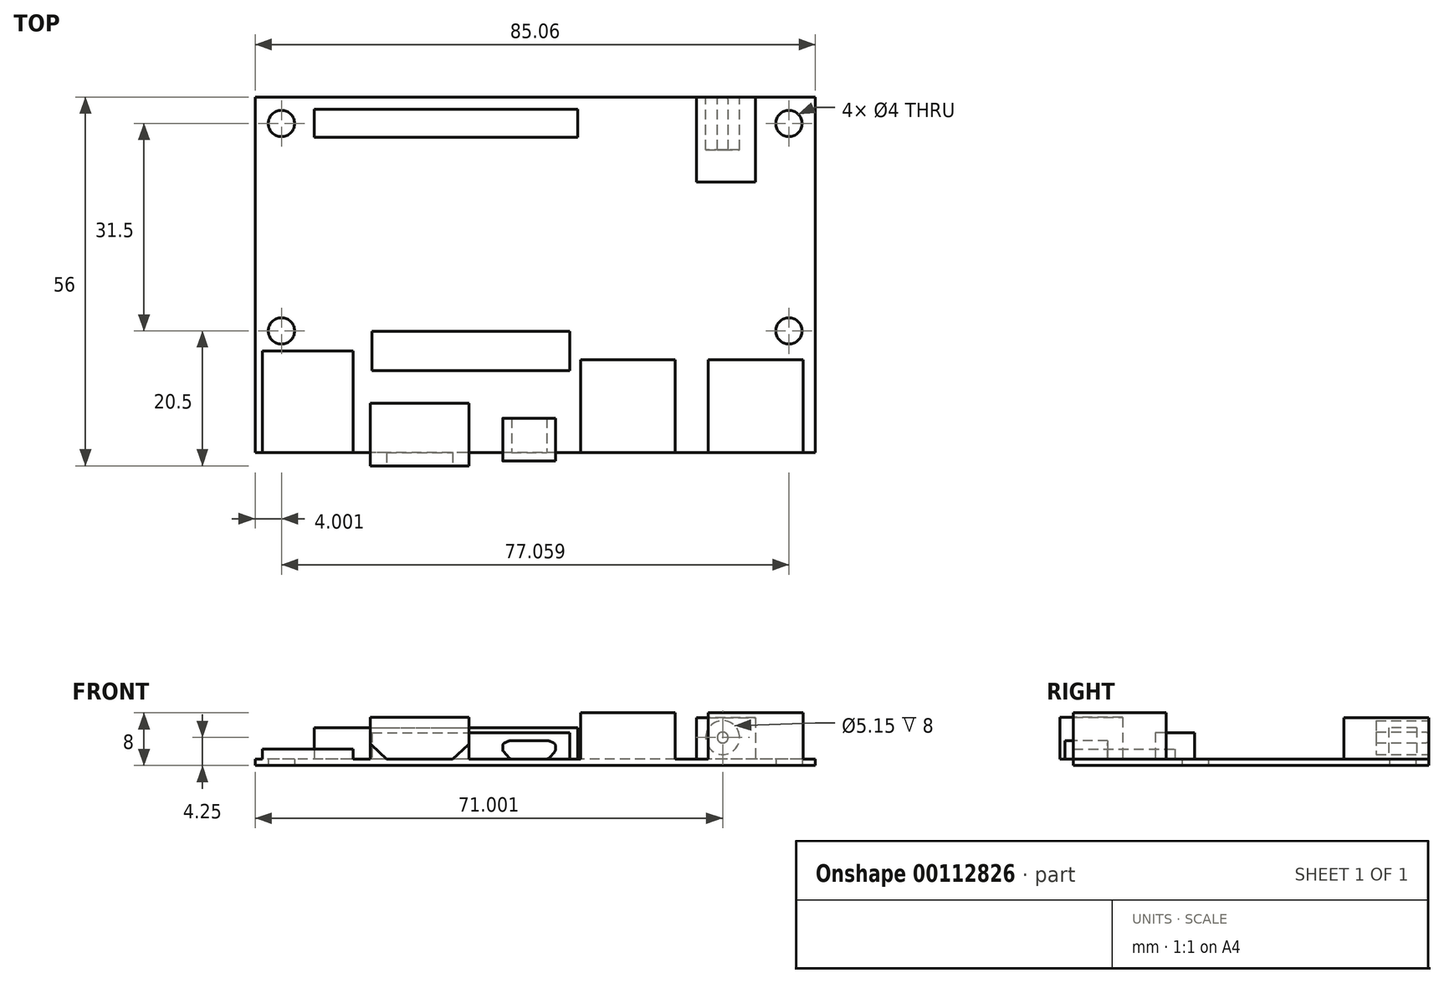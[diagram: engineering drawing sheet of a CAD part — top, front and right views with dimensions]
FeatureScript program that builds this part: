
annotation { "Feature Type Name" : "Feature", "Feature Type Description" : "" }
export const myFeature = defineFeature(function(context is Context, id is Id, definition is map)
    precondition{}
    {
        {
            var Q0;
            Q0=qCreatedBy(makeId("Top.planeOp"),FACE);
            var sketch = newSketch(context, id + "F0", { "sketchPlane" : qUnion([Q0])});
            skLineSegment(sketch, "E0.bottom", {"start": v(42.53, -27) * mm, "end": v(-42.53, -27) * mm});
            skLineSegment(sketch, "E0.top", {"start": v(42.53, 27) * mm, "end": v(-42.53, 27) * mm});
            skLineSegment(sketch, "E0.left", {"start": v(42.53, -27) * mm, "end": v(42.53, 27) * mm});
            skLineSegment(sketch, "E0.right", {"start": v(-42.53, -27) * mm, "end": v(-42.53, 27) * mm});
            skPoint(sketch, "E0.middle", {"position": v(0, 0) * mm});
            skLineSegment(sketch, "E1", {"start": v(-38.53, 27) * mm, "end": v(-38.53, -27) * mm, "construction": true});
            skLineSegment(sketch, "E2", {"start": v(38.53, 27) * mm, "end": v(38.53, -27) * mm, "construction": true});
            skLineSegment(sketch, "E3", {"start": v(-42.53, 23) * mm, "end": v(42.53, 23) * mm, "construction": true});
            skLineSegment(sketch, "E4", {"start": v(-42.53, -8.5) * mm, "end": v(42.53, -8.5) * mm, "construction": true});
            skPoint(sketch, "E5", {"position": v(-38.53, 23) * mm});
            skPoint(sketch, "E6", {"position": v(38.53, 23) * mm});
            skPoint(sketch, "E7", {"position": v(38.53, -8.5) * mm});
            skPoint(sketch, "E8", {"position": v(-38.53, -8.5) * mm});
            skCircle(sketch, "E9", {"center": v(-38.53, 23) * mm, "radius": 2 * mm});
            skCircle(sketch, "E10", {"center": v(38.53, 23) * mm, "radius": 2 * mm});
            skCircle(sketch, "E11", {"center": v(38.53, -8.5) * mm, "radius": 2 * mm});
            skCircle(sketch, "E12", {"center": v(-38.53, -8.5) * mm, "radius": 2 * mm});
            skSolve(sketch);
        }
        {
            var Q0;
            Q0=makeQuery(id+"F0.imprint","IMPRINT",FACE,{"disambiguationData":[TD([[makeQuery(id+"F0.imprint","IMPRINT",EDGE,{"derivedFrom":sQuery(id+"F0.wireOp",EDGE,"E0.bottom")}),-1.0]])]});
            var sketch = newSketch(context, id + "F1", { "sketchPlane" : qUnion([Q0])});
            skLineSegment(sketch, "E13.bottom", {"start": v(-35.03, 26.25) * mm, "end": v(7.97, 26.25) * mm, "construction": true});
            skLineSegment(sketch, "E13.top", {"start": v(-35.03, 19.75) * mm, "end": v(7.97, 19.75) * mm, "construction": true});
            skLineSegment(sketch, "E13.left", {"start": v(-35.03, 26.25) * mm, "end": v(-35.03, 19.75) * mm, "construction": true});
            skLineSegment(sketch, "E13.right", {"start": v(7.97, 26.25) * mm, "end": v(7.97, 19.75) * mm, "construction": true});
            skPoint(sketch, "E14", {"position": v(-35.03, 23) * mm});
            skLineSegment(sketch, "E15", {"start": v(-32.53, 26.25) * mm, "end": v(-32.53, 19.75) * mm, "construction": true});
            skPoint(sketch, "E16", {"position": v(-32.53, 23) * mm});
            skLineSegment(sketch, "E17.bottom", {"start": v(-33.53, 25.12) * mm, "end": v(6.47, 25.12) * mm});
            skLineSegment(sketch, "E17.top", {"start": v(-33.53, 20.88) * mm, "end": v(6.47, 20.88) * mm});
            skLineSegment(sketch, "E17.left", {"start": v(-33.53, 25.12) * mm, "end": v(-33.53, 20.87) * mm});
            skLineSegment(sketch, "E17.right", {"start": v(6.47, 25.12) * mm, "end": v(6.47, 20.87) * mm});
            skSolve(sketch);
        }
        {
            var Q0;
            Q0=makeQuery(id+"F0.imprint","IMPRINT",FACE,{"disambiguationData":[TD([[makeQuery(id+"F0.imprint","IMPRINT",EDGE,{"derivedFrom":sQuery(id+"F0.wireOp",EDGE,"E0.bottom")}),-1.0]])]});
            var sketch = newSketch(context, id + "F2", { "sketchPlane" : qUnion([Q0])});
            skLineSegment(sketch, "E18.0", {"start": v(42.53, 27) * mm, "end": v(-42.53, 27) * mm});
            skLineSegment(sketch, "E19", {"start": v(24.47, 27) * mm, "end": v(24.47, 14.1) * mm});
            skLineSegment(sketch, "E20", {"start": v(24.47, 14.1) * mm, "end": v(33.47, 14.1) * mm});
            skLineSegment(sketch, "E21", {"start": v(33.47, 14.1) * mm, "end": v(33.47, 27) * mm});
            skLineSegment(sketch, "E22", {"start": v(28.97, 14.1) * mm, "end": v(28.97, 27) * mm, "construction": true});
            skLineSegment(sketch, "E23.0", {"start": v(-42.53, -27) * mm, "end": v(-42.53, 27) * mm});
            skSolve(sketch);
        }
        {
            var Q0;
            Q0=makeQuery(id+"F0.imprint","IMPRINT",FACE,{"disambiguationData":[TD([[makeQuery(id+"F0.imprint","IMPRINT",EDGE,{"derivedFrom":sQuery(id+"F0.wireOp",EDGE,"E0.bottom")}),-1.0]])]});
            var sketch = newSketch(context, id + "F3", { "sketchPlane" : qUnion([Q0])});
            skLineSegment(sketch, "E24.0", {"start": v(-42.53, -27) * mm, "end": v(-42.53, 27) * mm});
            skLineSegment(sketch, "E25.0", {"start": v(42.53, -27) * mm, "end": v(42.53, 27) * mm});
            skLineSegment(sketch, "E26", {"start": v(-42.53, -11.55) * mm, "end": v(42.53, -11.55) * mm, "construction": true});
            skLineSegment(sketch, "E27.0", {"start": v(42.53, -27) * mm, "end": v(-42.53, -27) * mm});
            skLineSegment(sketch, "E28", {"start": v(-34.53, -27) * mm, "end": v(-34.53, -11.55) * mm, "construction": true});
            skLineSegment(sketch, "E29", {"start": v(-17.53, -27) * mm, "end": v(-17.53, -11.55) * mm, "construction": true});
            skLineSegment(sketch, "E30", {"start": v(-25.03, -27) * mm, "end": v(-25.03, -19.5) * mm});
            skLineSegment(sketch, "E31", {"start": v(-25.03, -19.5) * mm, "end": v(-10.03, -19.5) * mm});
            skLineSegment(sketch, "E32", {"start": v(-10.03, -19.5) * mm, "end": v(-10.03, -27) * mm});
            skLineSegment(sketch, "E33", {"start": v(-41.41, -27) * mm, "end": v(-41.41, -11.55) * mm});
            skLineSegment(sketch, "E34", {"start": v(-41.41, -11.55) * mm, "end": v(-27.64, -11.55) * mm});
            skLineSegment(sketch, "E35", {"start": v(-27.64, -11.55) * mm, "end": v(-27.64, -27) * mm});
            skLineSegment(sketch, "E36", {"start": v(-0.93, -11.55) * mm, "end": v(-0.93, -27) * mm, "construction": true});
            skLineSegment(sketch, "E37", {"start": v(-4.93, -27) * mm, "end": v(-4.93, -21.75) * mm});
            skLineSegment(sketch, "E38", {"start": v(-4.93, -21.75) * mm, "end": v(3.07, -21.75) * mm});
            skLineSegment(sketch, "E39", {"start": v(3.07, -21.75) * mm, "end": v(3.07, -27) * mm});
            skLineSegment(sketch, "E40", {"start": v(14.07, -27) * mm, "end": v(14.07, -11.55) * mm, "construction": true});
            skLineSegment(sketch, "E41", {"start": v(33.47, -27) * mm, "end": v(33.47, -11.55) * mm, "construction": true});
            skLineSegment(sketch, "E42", {"start": v(6.87, -27) * mm, "end": v(6.87, -12.9) * mm});
            skLineSegment(sketch, "E43", {"start": v(6.87, -12.9) * mm, "end": v(21.27, -12.9) * mm});
            skLineSegment(sketch, "E44", {"start": v(21.27, -12.9) * mm, "end": v(21.27, -27) * mm});
            skLineSegment(sketch, "E45", {"start": v(26.27, -27) * mm, "end": v(26.27, -12.9) * mm});
            skLineSegment(sketch, "E46", {"start": v(26.27, -12.9) * mm, "end": v(40.67, -12.9) * mm});
            skLineSegment(sketch, "E47", {"start": v(40.67, -12.9) * mm, "end": v(40.67, -27) * mm});
            skLineSegment(sketch, "E48", {"start": v(-25.03, -27) * mm, "end": v(-25.03, -29) * mm});
            skLineSegment(sketch, "E49", {"start": v(-25.03, -29) * mm, "end": v(-10.03, -29) * mm});
            skLineSegment(sketch, "E50", {"start": v(-10.03, -29) * mm, "end": v(-10.03, -27) * mm});
            skLineSegment(sketch, "E51", {"start": v(-4.93, -27) * mm, "end": v(-4.93, -28.25) * mm});
            skLineSegment(sketch, "E52", {"start": v(-4.93, -28.25) * mm, "end": v(3.07, -28.25) * mm});
            skLineSegment(sketch, "E53", {"start": v(3.07, -28.25) * mm, "end": v(3.07, -27) * mm});
            skSolve(sketch);
        }
        {
            var Q0;
            Q0=makeQuery(id+"F0.imprint","IMPRINT",FACE,{"disambiguationData":[TD([[makeQuery(id+"F0.imprint","IMPRINT",EDGE,{"derivedFrom":sQuery(id+"F0.wireOp",EDGE,"E0.bottom")}),-1.0]])]});
            var sketch = newSketch(context, id + "F4", { "sketchPlane" : qUnion([Q0])});
            skLineSegment(sketch, "E54.bottom", {"start": v(-24.76, -8.55) * mm, "end": v(5.24, -8.55) * mm});
            skLineSegment(sketch, "E54.top", {"start": v(-24.76, -14.55) * mm, "end": v(5.24, -14.55) * mm});
            skLineSegment(sketch, "E54.left", {"start": v(-24.76, -8.55) * mm, "end": v(-24.76, -14.55) * mm});
            skLineSegment(sketch, "E54.right", {"start": v(5.24, -8.55) * mm, "end": v(5.24, -14.55) * mm});
            skLineSegment(sketch, "E55.0", {"start": v(-21.38, -27) * mm, "end": v(-21.38, -11.55) * mm});
            skLineSegment(sketch, "E55.1", {"start": v(-42.53, -27) * mm, "end": v(-42.53, 27) * mm});
            skSolve(sketch);
        }
        {
            var Q0;
            Q0 = qSketchRegion(id + "F0", true);
            extrude(context, id + "F5", {"entities" : qUnion([Q0]), "depth" : 1 * mm});
        }
        {
            var Q0;
            {var subQ0=sQuery(id+"F3.wireOp",EDGE,"E45");Q0=makeQuery(id+"F3.imprint","IMPRINT",FACE,{"disambiguationData":[TD([[makeQuery(id+"F3.imprint","IMPRINT",EDGE,{"derivedFrom":subQ0}),-1.0]])]});}
            var Q1;
            {var subQ0=sQuery(id+"F3.wireOp",EDGE,"E42");Q1=makeQuery(id+"F3.imprint","IMPRINT",FACE,{"disambiguationData":[TD([[makeQuery(id+"F3.imprint","IMPRINT",EDGE,{"derivedFrom":subQ0}),-1.0]])]});}
            extrude(context, id + "F6", {"entities" : qUnion([Q0, Q1]), "operationType" : NewBodyOperationType.ADD, "depth" : 8 * mm});
        }
        {
            var Q0;
            {var subQ0=sQuery(id+"F3.wireOp",EDGE,"E51");Q0=makeQuery(id+"F3.imprint","IMPRINT",FACE,{"disambiguationData":[TD([[makeQuery(id+"F3.imprint","IMPRINT",EDGE,{"derivedFrom":subQ0}),1.0]])]});}
            var Q1;
            {var subQ0=sQuery(id+"F3.wireOp",EDGE,"E37");Q1=makeQuery(id+"F3.imprint","IMPRINT",FACE,{"disambiguationData":[TD([[makeQuery(id+"F3.imprint","IMPRINT",EDGE,{"derivedFrom":subQ0}),-1.0]])]});}
            extrude(context, id + "F7", {"entities" : qUnion([Q0, Q1]), "operationType" : NewBodyOperationType.ADD, "depth" : 3.75 * mm});
        }
        {
            var Q0;
            {var subQ0=sQuery(id+"F3.wireOp",EDGE,"E48");Q0=makeQuery(id+"F3.imprint","IMPRINT",FACE,{"disambiguationData":[TD([[makeQuery(id+"F3.imprint","IMPRINT",EDGE,{"derivedFrom":subQ0}),1.0]])]});}
            var Q1;
            {var subQ0=sQuery(id+"F3.wireOp",EDGE,"E30");Q1=makeQuery(id+"F3.imprint","IMPRINT",FACE,{"disambiguationData":[TD([[makeQuery(id+"F3.imprint","IMPRINT",EDGE,{"derivedFrom":subQ0}),-1.0]])]});}
            extrude(context, id + "F8", {"entities" : qUnion([Q0, Q1]), "operationType" : NewBodyOperationType.ADD, "depth" : 7.3 * mm});
        }
        {
            var Q0;
            {var subQ0=sQuery(id+"F3.wireOp",EDGE,"E33");Q0=makeQuery(id+"F3.imprint","IMPRINT",FACE,{"disambiguationData":[TD([[makeQuery(id+"F3.imprint","IMPRINT",EDGE,{"derivedFrom":subQ0}),-1.0]])]});}
            extrude(context, id + "F9", {"entities" : qUnion([Q0]), "operationType" : NewBodyOperationType.ADD, "depth" : 2.5 * mm});
        }
        {
            var Q0;
            {var subQ0=sQuery(id+"F2.wireOp",EDGE,"E19");Q0=makeQuery(id+"F2.imprint","IMPRINT",FACE,{"disambiguationData":[TD([[makeQuery(id+"F2.imprint","IMPRINT",EDGE,{"derivedFrom":subQ0}),1.0]])]});}
            extrude(context, id + "F10", {"entities" : qUnion([Q0]), "operationType" : NewBodyOperationType.ADD, "depth" : 7.25 * mm});
        }
        {
            var Q0;
            Q0 = qSketchRegion(id + "F1", true);
            extrude(context, id + "F11", {"entities" : qUnion([Q0]), "operationType" : NewBodyOperationType.ADD, "depth" : 5.75 * mm});
        }
        {
            var Q0;
            Q0 = qSketchRegion(id + "F4", true);
            extrude(context, id + "F12", {"entities" : qUnion([Q0]), "operationType" : NewBodyOperationType.ADD, "depth" : 5 * mm});
        }
        {
            var Q0;
            Q0=makeQuery(id+"F7.opExtrude","SWEPT_FACE",FACE,{"disambiguationData":[OSD([sQuery(id+"F3.wireOp",EDGE,"E52")])]});
            var sketch = newSketch(context, id + "F13", { "sketchPlane" : qUnion([Q0])});
            skPoint(sketch, "E56", {"position": v(-0.93, 0) * mm});
            skLineSegment(sketch, "E57", {"start": v(-4.93, 0) * mm, "end": v(-0.93, 0) * mm, "construction": true});
            skPoint(sketch, "E58", {"position": v(-2.93, 0) * mm});
            skLineSegment(sketch, "E59", {"start": v(-0.93, 0) * mm, "end": v(3.07, 0) * mm, "construction": true});
            skPoint(sketch, "E60", {"position": v(1.07, 0) * mm});
            skLineSegment(sketch, "E61", {"start": v(-4.8, 2.1) * mm, "end": v(-3.97, 1.17) * mm});
            skLineSegment(sketch, "E62", {"start": v(2.12, 1.17) * mm, "end": v(2.94, 2.08) * mm});
            skPoint(sketch, "E63", {"position": v(-3.94, 3.75) * mm});
            skPoint(sketch, "E64", {"position": v(2.09, 3.75) * mm});
            skLineSegment(sketch, "E65", {"start": v(-0.93, 0) * mm, "end": v(-0.93, 3.75) * mm, "construction": true});
            skLineSegment(sketch, "E66", {"start": v(-4.62, 3.47) * mm, "end": v(-4.08, 3.7) * mm});
            skLineSegment(sketch, "E67", {"start": v(2.77, 3.46) * mm, "end": v(2.22, 3.7) * mm});
            skLineSegment(sketch, "E68", {"start": v(-4.93, 2.24) * mm, "end": v(3.07, 2.22) * mm, "construction": true});
            skLineSegment(sketch, "E69", {"start": v(-4.93, 3.35) * mm, "end": v(3.07, 3.33) * mm, "construction": true});
            skLineSegment(sketch, "E70", {"start": v(-4.93, 3.01) * mm, "end": v(-4.93, 2.43) * mm});
            skLineSegment(sketch, "E71", {"start": v(3.07, 3) * mm, "end": v(3.07, 2.42) * mm});
            skLineSegment(sketch, "E72", {"start": v(-3.8, 3.75) * mm, "end": v(1.94, 3.75) * mm});
            skLineSegment(sketch, "E73", {"start": v(-2.73, 0) * mm, "end": v(0.87, 0) * mm});
            skPoint(sketch, "E74.visualSharp", {"position": v(3.07, 2.22) * mm});
            skArc(sketch, "E74.filletArc", {"start": v(2.94, 2.08) * mm, "mid": v(3.04, 2.24) * mm, "end": v(3.07, 2.42) * mm});
            skPoint(sketch, "E75.visualSharp", {"position": v(3.07, 3.33) * mm});
            skArc(sketch, "E75.filletArc", {"start": v(3.07, 3) * mm, "mid": v(2.99, 3.28) * mm, "end": v(2.77, 3.46) * mm});
            skArc(sketch, "E76.filletArc", {"start": v(2.22, 3.7) * mm, "mid": v(2.08, 3.74) * mm, "end": v(1.94, 3.75) * mm});
            skArc(sketch, "E77.filletArc", {"start": v(-3.8, 3.75) * mm, "mid": v(-3.94, 3.74) * mm, "end": v(-4.08, 3.7) * mm});
            skPoint(sketch, "E78.visualSharp", {"position": v(-4.93, 3.35) * mm});
            skArc(sketch, "E78.filletArc", {"start": v(-4.62, 3.47) * mm, "mid": v(-4.84, 3.3) * mm, "end": v(-4.93, 3.01) * mm});
            skPoint(sketch, "E79.visualSharp", {"position": v(-4.93, 2.24) * mm});
            skArc(sketch, "E79.filletArc", {"start": v(-4.93, 2.43) * mm, "mid": v(-4.9, 2.25) * mm, "end": v(-4.8, 2.1) * mm});
            skLineSegment(sketch, "E80.0", {"start": v(24.47, 1) * mm, "end": v(-42.53, 1) * mm});
            skLineSegment(sketch, "E81", {"start": v(-3.6, 1) * mm, "end": v(1.75, 1) * mm});
            skPoint(sketch, "E82.visualSharp", {"position": v(-3.82, 1) * mm});
            skArc(sketch, "E82.filletArc", {"start": v(-3.97, 1.17) * mm, "mid": v(-3.8, 1.04) * mm, "end": v(-3.6, 1) * mm});
            skPoint(sketch, "E83.visualSharp", {"position": v(1.97, 1) * mm});
            skArc(sketch, "E83.filletArc", {"start": v(1.75, 1) * mm, "mid": v(1.95, 1.04) * mm, "end": v(2.12, 1.17) * mm});
            skSolve(sketch);
        }
        {
            var Q0;
            Q0=makeQuery(id+"F13.imprint","IMPRINT",FACE,{"disambiguationData":[TD([[makeQuery(id+"F13.imprint","IMPRINT",EDGE,{"derivedFrom":sQuery(id+"F13.wireOp",EDGE,"E61")}),-1.0]])]});
            var Q1;
            Q1=makeQuery(id+"F13.imprint","IMPRINT",FACE,{"disambiguationData":[TD([[makeQuery(id+"F13.imprint","IMPRINT",EDGE,{"derivedFrom":sQuery(id+"F13.wireOp",EDGE,"E66")}),1.0]])]});
            var Q2;
            Q2=makeQuery(id+"F13.imprint","IMPRINT",FACE,{"disambiguationData":[TD([[makeQuery(id+"F13.imprint","IMPRINT",EDGE,{"derivedFrom":sQuery(id+"F13.wireOp",EDGE,"E67")}),-1.0]])]});
            var Q3;
            Q3=makeQuery(id+"F13.imprint","IMPRINT",FACE,{"disambiguationData":[TD([[makeQuery(id+"F13.imprint","IMPRINT",EDGE,{"derivedFrom":sQuery(id+"F13.wireOp",EDGE,"E62")}),-1.0]])]});
            var Q4;
            {var subQ8=sQuery(id+"F13.wireOp",EDGE,"a18c98a6-a4a7-4cf6-845e-3db316127b87.filletArc");Q4=makeQuery(id+"F13.imprint","IMPRINT",FACE,{"disambiguationData":[TD([[makeQuery(id+"F13.imprint","IMPRINT",EDGE,{"derivedFrom":subQ8}),-1.0]])]});}
            var Q5;
            {var subQ6=sQuery(id+"F13.wireOp",EDGE,"c999dc16-cddd-47d2-9ace-dcb4409ff7b4.filletArc");Q5=makeQuery(id+"F13.imprint","IMPRINT",FACE,{"disambiguationData":[TD([[makeQuery(id+"F13.imprint","IMPRINT",EDGE,{"derivedFrom":subQ6}),-1.0]])]});}
            var Q6;
            {var subQ9=sQuery(id+"F13.wireOp",EDGE,"E73");Q6=makeQuery(id+"F13.imprint","IMPRINT",FACE,{"disambiguationData":[TD([[makeQuery(id+"F13.imprint","IMPRINT",EDGE,{"derivedFrom":subQ9}),1.0]])]});}
            var Q7;
            {var subQ0=sQuery(id+"F3.wireOp",EDGE,"E51");var subQ1=sQuery(id+"F3.wireOp",EDGE,"E37");var subQ2=makeQuery(id+"F7.opExtrude","SWEPT_FACE",FACE,{"disambiguationData":[OSD([subQ1,subQ0])]});var subQ8=sQuery(id+"F0.wireOp",EDGE,"E0.right");var subQ11=sQuery(id+"F0.wireOp",EDGE,"E0.bottom");var subQ16=sQuery(id+"F3.wireOp",EDGE,"E27.0");Q7=makeQuery(id+"F8.boolean.opBoolean","SPLIT",FACE,{"disambiguationData":[TD([subQ2])],"derivedFrom":makeQuery(id+"F7.boolean.opBoolean","SPLIT",FACE,{"disambiguationData":[TD([makeQuery(id+"F5.opExtrude","SWEPT_FACE",FACE,{"disambiguationData":[OSD([subQ8])]})])],"derivedFrom":makeQuery(id+"F6.boolean.opBoolean","MERGE",FACE,{"derivedFrom":[makeQuery(id+"F5.opExtrude","SWEPT_FACE",FACE,{"disambiguationData":[OSD([subQ11])]}),makeQuery(id+"F6.opExtrude","SWEPT_FACE",FACE,{"disambiguationData":[OSD([subQ16]),TDD([makeQuery(id+"F3.imprint","IMPRINT",EDGE,{"disambiguationData":[TD([[makeQuery(id+"F3.imprint","INTERSECT",VERTEX,{"derivedFrom":[subQ16,sQuery(id+"F3.wireOp",EDGE,"E45")]}),1.0]])],"derivedFrom":subQ16})])]}),makeQuery(id+"F6.opExtrude","SWEPT_FACE",FACE,{"disambiguationData":[OSD([subQ16]),TDD([makeQuery(id+"F3.imprint","IMPRINT",EDGE,{"disambiguationData":[TD([[makeQuery(id+"F3.imprint","INTERSECT",VERTEX,{"derivedFrom":[subQ16,sQuery(id+"F3.wireOp",EDGE,"E42")]}),1.0]])],"derivedFrom":subQ16})])]})]})})});}
            extrude(context, id + "F14", {"entities" : qUnion([Q0, Q1, Q2, Q3, Q4, Q5, Q6]), "operationType" : NewBodyOperationType.REMOVE, "endBound" : BoundingType.UP_TO_SURFACE, "oppositeDirection" : true, "endBoundEntityFace" : qUnion([Q7]), "depth" : 25 * mm});
        }
        {
            var Q0;
            Q0=makeQuery(id+"F14.boolean.opBoolean","COPY",FACE,{"derivedFrom":makeQuery(id+"F14.opExtrude","CAP_FACE",FACE,{"disambiguationData":[OSD([sQuery(id+"F3.wireOp",EDGE,"E51"),sQuery(id+"F3.wireOp",EDGE,"E52"),sQuery(id+"F13.wireOp",EDGE,"E66"),sQuery(id+"F13.wireOp",EDGE,"E77.filletArc"),sQuery(id+"F13.wireOp",EDGE,"E78.filletArc")])],"isStart":false})});
            var Q1;
            Q1=makeQuery(id+"F14.boolean.opBoolean","COPY",FACE,{"derivedFrom":makeQuery(id+"F14.opExtrude","CAP_FACE",FACE,{"disambiguationData":[OSD([sQuery(id+"F3.wireOp",EDGE,"E52"),sQuery(id+"F3.wireOp",EDGE,"E53"),sQuery(id+"F13.wireOp",EDGE,"E67"),sQuery(id+"F13.wireOp",EDGE,"E75.filletArc"),sQuery(id+"F13.wireOp",EDGE,"E76.filletArc")])],"isStart":false})});
            var Q2;
            {var subQ0=sQuery(id+"F13.wireOp",EDGE,"E79.filletArc");Q2=makeQuery(id+"F13.imprint","IMPRINT",FACE,{"disambiguationData":[TD([[makeQuery(id+"F13.imprint","IMPRINT",EDGE,{"derivedFrom":subQ0}),-1.0]])]});}
            var Q3;
            {var subQ0=sQuery(id+"F13.wireOp",EDGE,"E74.filletArc");Q3=makeQuery(id+"F13.imprint","IMPRINT",FACE,{"disambiguationData":[TD([[makeQuery(id+"F13.imprint","IMPRINT",EDGE,{"derivedFrom":subQ0}),-1.0]])]});}
            var Q4;
            Q4=makeQuery(id+"F7.opExtrude","SWEPT_FACE",FACE,{"disambiguationData":[OSD([sQuery(id+"F3.wireOp",EDGE,"E38")])]});
            extrude(context, id + "F15", {"entities" : qUnion([Q0, Q1, Q2, Q3]), "operationType" : NewBodyOperationType.REMOVE, "endBound" : BoundingType.UP_TO_SURFACE, "oppositeDirection" : true, "endBoundEntityFace" : qUnion([Q4]), "depth" : 25 * mm});
        }
        {
            var Q0;
            Q0=makeQuery(id+"F8.opExtrude","SWEPT_FACE",FACE,{"disambiguationData":[OSD([sQuery(id+"F3.wireOp",EDGE,"E49")])]});
            var sketch = newSketch(context, id + "F16", { "sketchPlane" : qUnion([Q0])});
            skLineSegment(sketch, "E84.0", {"start": v(-25.03, 7.3) * mm, "end": v(-10.03, 7.3) * mm});
            skLineSegment(sketch, "E85.0", {"start": v(-10.03, 7.3) * mm, "end": v(-10.03, 3.52) * mm});
            skLineSegment(sketch, "E86.0", {"start": v(-25.03, 7.3) * mm, "end": v(-25.03, 3.52) * mm});
            skLineSegment(sketch, "E87.0", {"start": v(24.47, 1) * mm, "end": v(-42.53, 1) * mm});
            skLineSegment(sketch, "E88.0", {"start": v(-25.03, 0) * mm, "end": v(-10.03, 0) * mm});
            skLineSegment(sketch, "E89", {"start": v(-17.53, 7.3) * mm, "end": v(-17.53, 1) * mm, "construction": true});
            skPoint(sketch, "E90", {"position": v(-12.53, 1) * mm});
            skPoint(sketch, "E91", {"position": v(-22.53, 1) * mm});
            skLineSegment(sketch, "E92", {"start": v(-24.87, 3.15) * mm, "end": v(-22.53, 1) * mm});
            skLineSegment(sketch, "E93", {"start": v(-12.53, 1) * mm, "end": v(-10.2, 3.15) * mm});
            skLineSegment(sketch, "E94.trimOffspring", {"start": v(-10.03, 1) * mm, "end": v(-10.03, 0) * mm});
            skLineSegment(sketch, "E95.trimOffspring", {"start": v(-25.03, 1) * mm, "end": v(-25.03, 0) * mm});
            skPoint(sketch, "E96.visualSharp", {"position": v(-25.03, 3.3) * mm});
            skArc(sketch, "E96.filletArc", {"start": v(-25.03, 3.52) * mm, "mid": v(-24.99, 3.32) * mm, "end": v(-24.87, 3.15) * mm});
            skPoint(sketch, "E97.visualSharp", {"position": v(-10.03, 3.3) * mm});
            skArc(sketch, "E97.filletArc", {"start": v(-10.2, 3.15) * mm, "mid": v(-10.07, 3.32) * mm, "end": v(-10.03, 3.52) * mm});
            skSolve(sketch);
        }
        {
            var Q0;
            {var subQ0=sQuery(id+"F16.wireOp",EDGE,"E92");Q0=makeQuery(id+"F16.imprint","IMPRINT",FACE,{"disambiguationData":[TD([[makeQuery(id+"F16.imprint","IMPRINT",EDGE,{"derivedFrom":subQ0}),-1.0]])]});}
            var Q1;
            {var subQ0=sQuery(id+"F16.wireOp",EDGE,"E93");Q1=makeQuery(id+"F16.imprint","IMPRINT",FACE,{"disambiguationData":[TD([[makeQuery(id+"F16.imprint","IMPRINT",EDGE,{"derivedFrom":subQ0}),-1.0]])]});}
            var Q2;
            {var subQ3=sQuery(id+"F16.wireOp",EDGE,"E88.0");Q2=makeQuery(id+"F16.imprint","IMPRINT",FACE,{"disambiguationData":[TD([[makeQuery(id+"F16.imprint","IMPRINT",EDGE,{"derivedFrom":subQ3}),1.0]])]});}
            var Q3;
            {var subQ0=sQuery(id+"F3.wireOp",EDGE,"E53");var subQ1=sQuery(id+"F3.wireOp",EDGE,"E52");var subQ2=sQuery(id+"F3.wireOp",EDGE,"E51");var subQ3=sQuery(id+"F3.wireOp",EDGE,"E37");var subQ4=makeQuery(id+"F7.opExtrude","SWEPT_FACE",FACE,{"disambiguationData":[OSD([subQ3,subQ2])]});var subQ11=sQuery(id+"F0.wireOp",EDGE,"E0.right");var subQ12=sQuery(id+"F0.wireOp",EDGE,"E0.left");var subQ14=sQuery(id+"F0.wireOp",EDGE,"E0.bottom");var subQ19=sQuery(id+"F3.wireOp",EDGE,"E42");var subQ20=sQuery(id+"F3.wireOp",EDGE,"E27.0");var subQ22=sQuery(id+"F3.wireOp",EDGE,"E45");var subQ24=makeQuery(id+"F6.boolean.opBoolean","MERGE",FACE,{"derivedFrom":[makeQuery(id+"F5.opExtrude","SWEPT_FACE",FACE,{"disambiguationData":[OSD([subQ14])]}),makeQuery(id+"F6.opExtrude","SWEPT_FACE",FACE,{"disambiguationData":[OSD([subQ20]),TDD([makeQuery(id+"F3.imprint","IMPRINT",EDGE,{"disambiguationData":[TD([[makeQuery(id+"F3.imprint","INTERSECT",VERTEX,{"derivedFrom":[subQ20,subQ22]}),1.0]])],"derivedFrom":subQ20})])]}),makeQuery(id+"F6.opExtrude","SWEPT_FACE",FACE,{"disambiguationData":[OSD([subQ20]),TDD([makeQuery(id+"F3.imprint","IMPRINT",EDGE,{"disambiguationData":[TD([[makeQuery(id+"F3.imprint","INTERSECT",VERTEX,{"derivedFrom":[subQ20,subQ19]}),1.0]])],"derivedFrom":subQ20})])]})]});Q3=makeQuery(id+"F14.boolean.opBoolean","MERGE",FACE,{"derivedFrom":[makeQuery(id+"F7.boolean.opBoolean","SPLIT",FACE,{"disambiguationData":[TD([makeQuery(id+"F5.opExtrude","SWEPT_FACE",FACE,{"disambiguationData":[OSD([subQ12])]})])],"derivedFrom":subQ24}),makeQuery(id+"F8.boolean.opBoolean","SPLIT",FACE,{"disambiguationData":[TD([subQ4])],"derivedFrom":makeQuery(id+"F7.boolean.opBoolean","SPLIT",FACE,{"disambiguationData":[TD([makeQuery(id+"F5.opExtrude","SWEPT_FACE",FACE,{"disambiguationData":[OSD([subQ11])]})])],"derivedFrom":subQ24})}),makeQuery(id+"F14.opExtrude","CAP_FACE",FACE,{"disambiguationData":[OSD([subQ2,subQ1,subQ0,sQuery(id+"F13.wireOp",EDGE,"E61"),sQuery(id+"F13.wireOp",EDGE,"E62"),sQuery(id+"F13.wireOp",EDGE,"E73"),sQuery(id+"F13.wireOp",EDGE,"E74.filletArc"),sQuery(id+"F13.wireOp",EDGE,"E79.filletArc"),sQuery(id+"F13.wireOp",EDGE,"E81"),sQuery(id+"F13.wireOp",EDGE,"E82.filletArc"),sQuery(id+"F13.wireOp",EDGE,"E83.filletArc")])],"isStart":false})]});}
            extrude(context, id + "F17", {"entities" : qUnion([Q0, Q1, Q2]), "operationType" : NewBodyOperationType.REMOVE, "endBound" : BoundingType.UP_TO_SURFACE, "oppositeDirection" : true, "endBoundEntityFace" : qUnion([Q3]), "depth" : 25 * mm});
        }
        {
            var Q0;
            Q0=makeQuery(id+"F10.boolean.opBoolean","MERGE",FACE,{"derivedFrom":[makeQuery(id+"F5.opExtrude","SWEPT_FACE",FACE,{"disambiguationData":[OSD([sQuery(id+"F0.wireOp",EDGE,"E0.top")])]}),makeQuery(id+"F10.opExtrude","SWEPT_FACE",FACE,{"disambiguationData":[OSD([sQuery(id+"F2.wireOp",EDGE,"E18.0")])]})]});
            var sketch = newSketch(context, id + "F18", { "sketchPlane" : qUnion([Q0])});
            skLineSegment(sketch, "E98", {"start": v(-28.47, 7.25) * mm, "end": v(-28.47, 1) * mm, "construction": true});
            skCircle(sketch, "E99", {"center": v(-28.47, 4.25) * mm, "radius": 2.58 * mm});
            skCircle(sketch, "E100", {"center": v(-28.47, 4.25) * mm, "radius": 0.82 * mm});
            skLineSegment(sketch, "E101", {"start": v(-33.47, 7.25) * mm, "end": v(-24.47, 7.25) * mm});
            skSolve(sketch);
        }
        {
            var Q0;
            Q0=makeQuery(id+"F18.imprint","IMPRINT",FACE,{"disambiguationData":[TD([[makeQuery(id+"F18.imprint","IMPRINT",EDGE,{"derivedFrom":sQuery(id+"F18.wireOp",EDGE,"E99")}),1.0]])]});
            extrude(context, id + "F19", {"entities" : qUnion([Q0]), "operationType" : NewBodyOperationType.REMOVE, "oppositeDirection" : true, "depth" : 8 * mm});
        }
        {
            var Q0;
            Q0=makeQuery(id+"F19.boolean.opBoolean","SPLIT",FACE,{"disambiguationData":[TD([makeQuery(id+"F19.opExtrude","SWEPT_FACE",FACE,{"disambiguationData":[OSD([sQuery(id+"F18.wireOp",EDGE,"E100")])]})])],"derivedFrom":makeQuery(id+"F10.boolean.opBoolean","MERGE",FACE,{"derivedFrom":[makeQuery(id+"F5.opExtrude","SWEPT_FACE",FACE,{"disambiguationData":[OSD([sQuery(id+"F0.wireOp",EDGE,"E0.top")])]}),makeQuery(id+"F10.opExtrude","SWEPT_FACE",FACE,{"disambiguationData":[OSD([sQuery(id+"F2.wireOp",EDGE,"E18.0")])]})]})});
            fillet(context, id + "F20", {"entities" : qUnion([Q0]), "radius" : 0.4 * mm, "tangentPropagation" : true, "allowEdgeOverflow" : false});
        }
    });
